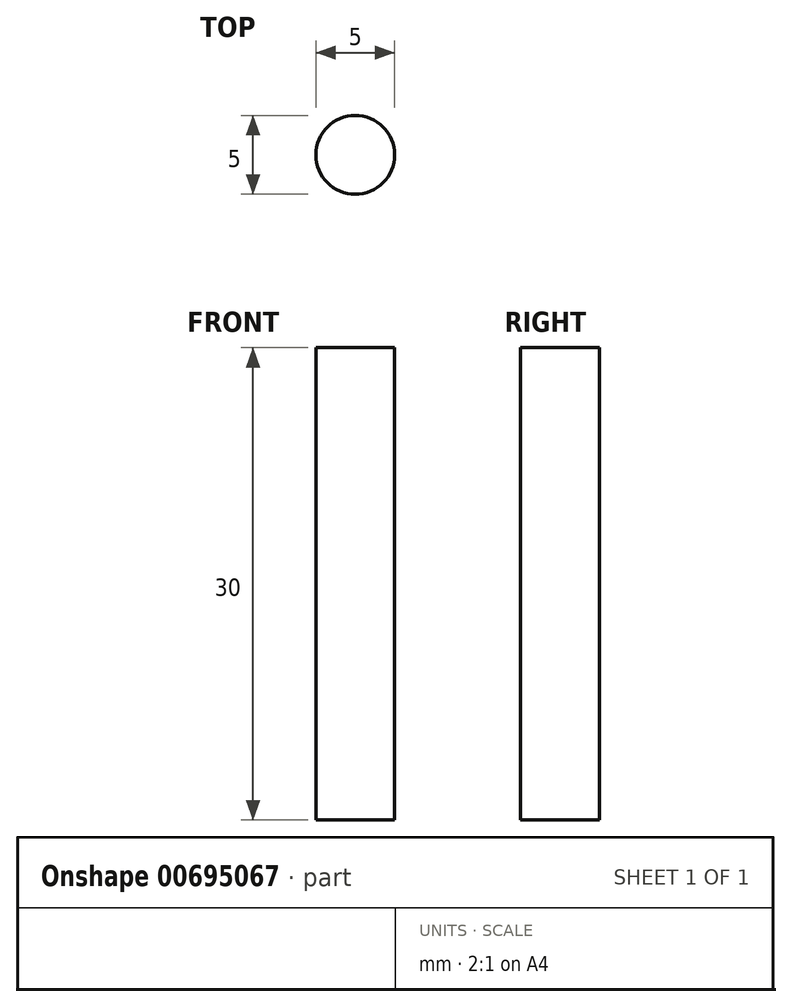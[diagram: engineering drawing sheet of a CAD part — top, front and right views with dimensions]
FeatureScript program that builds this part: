
annotation { "Feature Type Name" : "Feature", "Feature Type Description" : "" }
export const myFeature = defineFeature(function(context is Context, id is Id, definition is map)
    precondition{}
    {
        {
            var Q0;
            Q0=qCreatedBy(makeId("Top.planeOp"),FACE);
            var sketch = newSketch(context, id + "F0", { "sketchPlane" : qUnion([Q0])});
            skCircle(sketch, "E0", {"center": v(0, 0) * mm, "radius": 2.5 * mm});
            skSolve(sketch);
        }
        {
            var Q0;
            Q0 = qSketchRegion(id + "F0", true);
            extrude(context, id + "F1", {"entities" : qUnion([Q0]), "depth" : 30 * mm, "offsetDistance" : 25 * mm});
        }
    });
